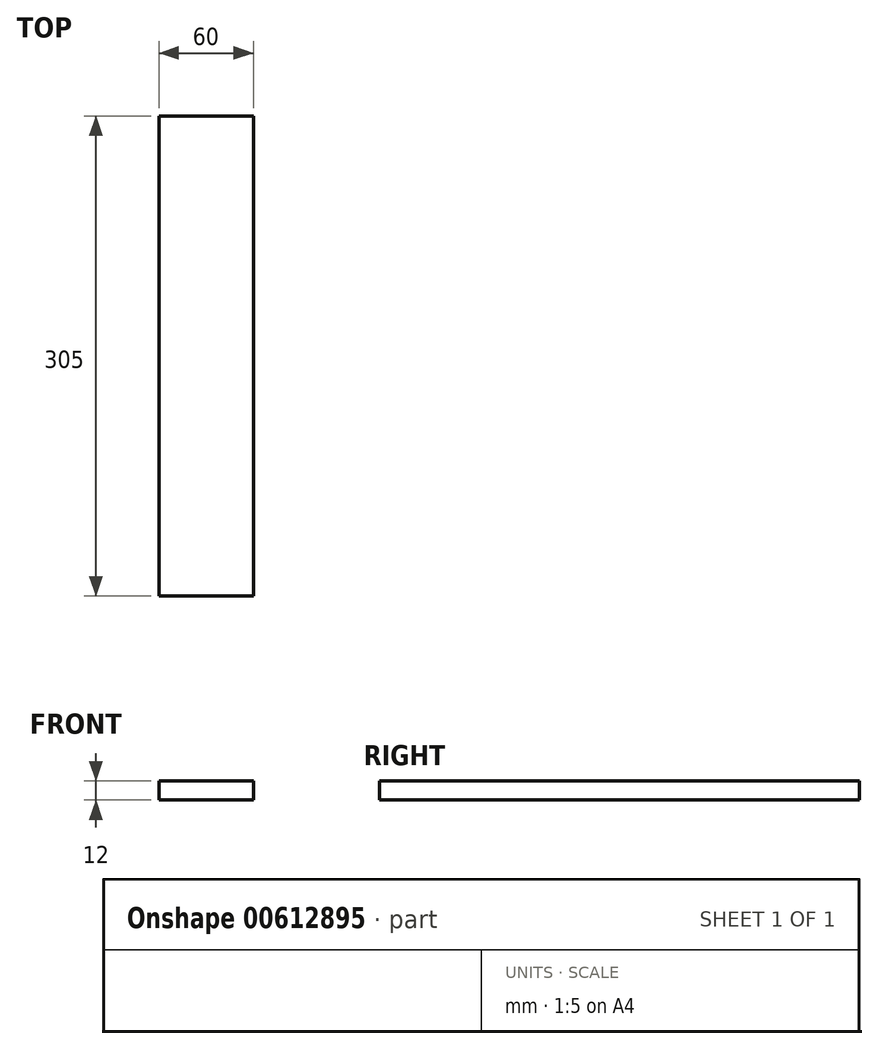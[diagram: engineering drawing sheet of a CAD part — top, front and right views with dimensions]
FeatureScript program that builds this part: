
annotation { "Feature Type Name" : "Feature", "Feature Type Description" : "" }
export const myFeature = defineFeature(function(context is Context, id is Id, definition is map)
    precondition{}
    {
        {
            var Q0;
            Q0=qCreatedBy(makeId("Top.planeOp"),FACE);
            var sketch = newSketch(context, id + "F0", { "sketchPlane" : qUnion([Q0])});
            skLineSegment(sketch, "E0.bottom", {"start": v(30, 152.5) * mm, "end": v(-30, 152.5) * mm});
            skLineSegment(sketch, "E0.top", {"start": v(30, -152.5) * mm, "end": v(-30, -152.5) * mm});
            skLineSegment(sketch, "E0.left", {"start": v(30, 152.5) * mm, "end": v(30, -152.5) * mm});
            skLineSegment(sketch, "E0.right", {"start": v(-30, 152.5) * mm, "end": v(-30, -152.5) * mm});
            skPoint(sketch, "E0.middle", {"position": v(0, 0) * mm});
            skSolve(sketch);
        }
        {
            var Q0;
            Q0=makeQuery(id+"F0.imprint","IMPRINT",FACE,{"disambiguationData":[TD([[makeQuery(id+"F0.imprint","IMPRINT",EDGE,{"derivedFrom":sQuery(id+"F0.wireOp",EDGE,"E0.bottom")}),1.0]])]});
            extrude(context, id + "F1", {"entities" : qUnion([Q0]), "depth" : 12 * mm, "offsetDistance" : 25 * mm});
        }
    });
